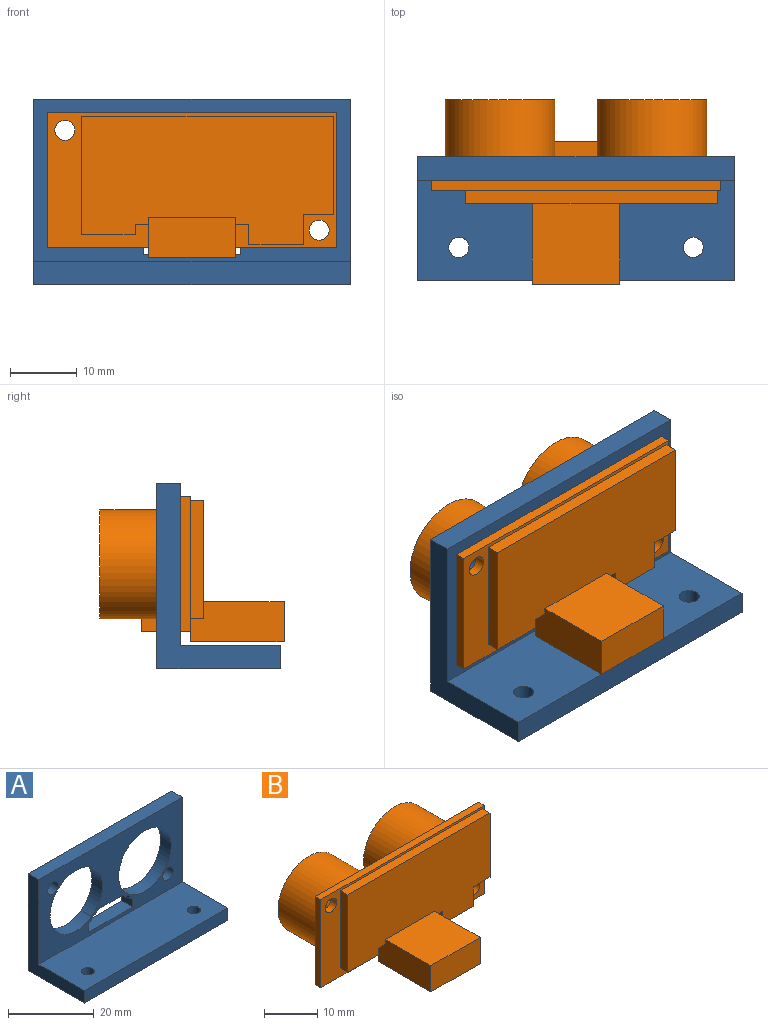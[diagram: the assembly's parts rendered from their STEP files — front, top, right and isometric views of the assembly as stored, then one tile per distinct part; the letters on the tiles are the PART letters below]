
ASSEMBLY  parts=2 mates=1
PART A: 26 faces, bbox 47.3x18.5x27.7 mm
  f0: plane 27.7x18.5mm, normal (-1,0,0), area 149.5mm2, adj f1,f19,f20,f21,f22,f23
  f1: plane 47.26x3.5mm, normal (0,0,1), area 165.4mm2, adj f0,f2,f20,f21
  f2: plane 27.7x18.5mm, normal (1,0,0), area 149.5mm2, adj f1,f19,f20,f21,f22,f23
  f3: plane 3.5x2.44mm, normal (1,0,0), area 8.5mm2, adj f4,f18,f20,f21
  f4: plane 14.5x3.5mm, normal (0,0,1), area 50.8mm2, adj f3,f5,f20,f21
  f5: plane 3.5x2.44mm, normal (-1,0,0), area 8.5mm2, adj f4,f6,f20,f21
  f6: cylinder r=9.57mm len=3.5mm, axis (0,-1,0), area 4mm2, adj f5,f7,f20,f21
  f7: plane 3.5x1.01mm, normal (-1,0,0), area 3.5mm2, adj f6,f8,f20,f21
  f8: plane 3.5x1.34mm, normal (0,0,-1), area 4.7mm2, adj f7,f9,f20,f21
  f9: cylinder r=9.57mm len=3.5mm, axis (0,-1,0), area 4.8mm2, adj f8,f10,f20,f21
  f10: plane 7.9x3.5mm, normal (0,0,-1), area 27.7mm2, adj f9,f11,f20,f21
  f11: cylinder r=9.57mm len=3.5mm, axis (0,-1,0), area 4.8mm2, adj f10,f12,f20,f21
  f12: plane 3.5x1.34mm, normal (0,0,-1), area 4.7mm2, adj f11,f13,f20,f21
  f13: plane 3.5x1.01mm, normal (1,0,0), area 3.5mm2, adj f12,f18,f20,f21
  f14: cylinder r=8.68mm len=17.35mm, axis (0,-1,0), area 190.8mm2, adj f20,f21
  f15: cylinder r=8.68mm len=17.35mm, axis (0,-1,0), area 190.8mm2, adj f20,f21
  f16: cylinder r=1.75mm len=3.5mm, axis (0,-1,0), area 38.5mm2, adj f20,f21
  f17: cylinder r=1.75mm len=3.5mm, axis (0,-1,0), area 38.5mm2, adj f20,f21
  f18: cylinder r=9.57mm len=3.5mm, axis (0,-1,0), area 4mm2, adj f3,f13,f20,f21
  f19: plane 47.26x18.5mm, normal (0,0,-1), area 860.2mm2, adj f0,f2,f20,f23,f24,f25
  f20: plane 47.26x27.7mm, normal (0,1,0), area 752.8mm2, adj f0,f1,f2,f3,f4,f5,f6,f7
  f21: plane 47.26x24.2mm, normal (0,-1,0), area 587.4mm2, adj f0,f1,f2,f3,f4,f5,f6,f7
  f22: plane 47.26x15mm, normal (0,0,1), area 694.8mm2, adj f0,f2,f21,f23,f24,f25
  f23: plane 47.26x3.5mm, normal (0,-1,0), area 165.4mm2, adj f0,f2,f19,f22
  f24: cylinder r=1.5mm len=3.5mm, axis (0,0,1), area 33mm2, adj f19,f22
  f25: cylinder r=1.5mm len=3.5mm, axis (0,0,1), area 33mm2, adj f19,f22
PART B: 34 faces, bbox 43.3x27.5x21.7 mm
  f0: plane 43.26x20.2mm, normal (0,-1,0), area 175.3mm2, adj f1,f2,f3,f4,f5,f6,f12,f14
  f1: plane 20.2x1.5mm, normal (1,0,0), area 30.3mm2, adj f0,f2,f5,f7
  f2: plane 43.26x1.5mm, normal (0,0,1), area 64.9mm2, adj f0,f1,f3,f7
  f3: plane 20.2x1.5mm, normal (-1,0,0), area 30.3mm2, adj f0,f2,f5,f7
  f4: cylinder r=1.5mm len=3mm, axis (0,1,0), area 14.1mm2, adj f0,f7
  f5: plane 43.26x7.3mm, normal (0,0,-1), area 137.4mm2, adj f0,f1,f3,f7,f17,f31,f32,f33
  f6: cylinder r=1.5mm len=3mm, axis (0,1,0), area 14.1mm2, adj f0,f7
  f7: plane 43.26x20.2mm, normal (0,1,0), area 402.3mm2, adj f1,f2,f3,f4,f5,f6,f8,f10
  f8: cylinder r=8.18mm len=16.35mm, axis (0,-1,0), area 616.4mm2, adj f7,f9
  f9: plane 16.35x16.35mm, normal (0,1,0), area 210mm2, adj f8
  f10: cylinder r=8.18mm len=16.35mm, axis (0,-1,0), area 616.4mm2, adj f7,f11
  f11: plane 16.35x16.35mm, normal (0,1,0), area 210mm2, adj f10
  f12: plane 14x6mm, normal (1,0,0), area 82mm2, adj f0,f13,f15,f16,f17,f20,f29
  f13: plane 13x12mm, normal (0,0,1), area 156mm2, adj f12,f14,f16,f29
  f14: plane 14x6mm, normal (-1,0,0), area 82mm2, adj f0,f13,f15,f16,f17,f19,f29
  f15: plane 14x13mm, normal (0,0,-1), area 182mm2, adj f12,f14,f16,f17
  f16: plane 13x6mm, normal (0,-1,0), area 78mm2, adj f12,f13,f14,f15
  f17: plane 13x1.5mm, normal (0,1,0), area 19.5mm2, adj f5,f12,f14,f15
  f18: plane 2x1.5mm, normal (1,0,0), area 3mm2, adj f0,f19,f28,f29
  f19: plane 2x2mm, normal (0,0,-1), area 4mm2, adj f0,f14,f18,f29
  f20: plane 2x2mm, normal (0,0,-1), area 4mm2, adj f0,f12,f21,f29
  f21: plane 3x2mm, normal (-1,0,0), area 6mm2, adj f0,f20,f22,f29
  f22: plane 8.13x2mm, normal (0,0,-1), area 16.3mm2, adj f0,f21,f23,f29
  f23: plane 4.5x2mm, normal (1,0,0), area 9mm2, adj f0,f22,f24,f29
  f24: plane 4.5x2mm, normal (0,0,-1), area 9mm2, adj f0,f23,f25,f29
  f25: plane 14.7x2mm, normal (1,0,0), area 29.4mm2, adj f0,f24,f26,f29
  f26: plane 37.61x2mm, normal (0,0,1), area 75.2mm2, adj f0,f25,f27,f29
  f27: plane 17.7x2mm, normal (-1,0,0), area 35.4mm2, adj f0,f26,f28,f29
  f28: plane 7.98x2mm, normal (0,0,-1), area 16mm2, adj f0,f18,f27,f29
  f29: plane 37.61x19.2mm, normal (0,-1,0), area 625.9mm2, adj f12,f13,f14,f18,f19,f20,f21,f22
  f30: plane 12.5x5.8mm, normal (0,0,1), area 72.5mm2, adj f7,f31,f32,f33
  f31: plane 5.8x3mm, normal (1,0,0), area 17.4mm2, adj f5,f7,f30,f33
  f32: plane 5.8x3mm, normal (-1,0,0), area 17.4mm2, adj f5,f7,f30,f33
  f33: plane 12.5x3mm, normal (0,1,0), area 37.5mm2, adj f5,f30,f31,f32
PLACE A at identity
PLACE B at identity
MATE fastened B.f6 <-> A.f16  axis (0,1,0) through (-18.98,0,7.45)mm
